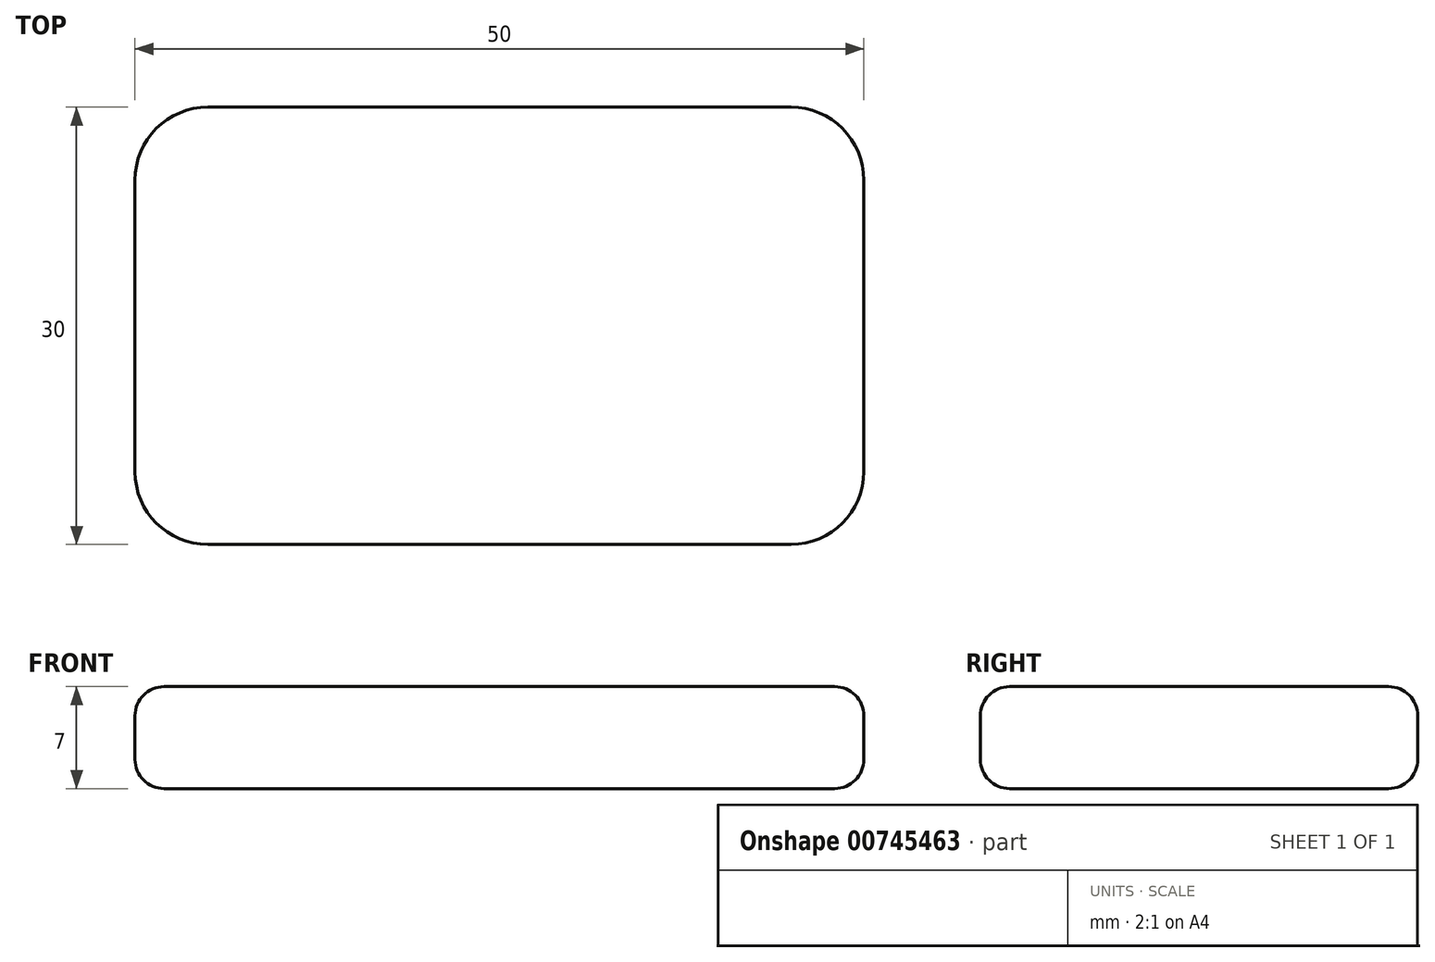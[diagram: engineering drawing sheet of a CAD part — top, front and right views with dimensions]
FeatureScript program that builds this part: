
annotation { "Feature Type Name" : "Feature", "Feature Type Description" : "" }
export const myFeature = defineFeature(function(context is Context, id is Id, definition is map)
    precondition{}
    {
        {
            var Q0;
            Q0=qCreatedBy(makeId("Top.planeOp"),FACE);
            var sketch = newSketch(context, id + "F0", { "sketchPlane" : qUnion([Q0])});
            skLineSegment(sketch, "E0.bottom", {"start": v(25, -15) * mm, "end": v(-25, -15) * mm});
            skLineSegment(sketch, "E0.top", {"start": v(25, 15) * mm, "end": v(-25, 15) * mm});
            skLineSegment(sketch, "E0.left", {"start": v(25, -15) * mm, "end": v(25, 15) * mm});
            skLineSegment(sketch, "E0.right", {"start": v(-25, -15) * mm, "end": v(-25, 15) * mm});
            skPoint(sketch, "E0.middle", {"position": v(0, 0) * mm});
            skSolve(sketch);
        }
        {
            var Q0;
            Q0=makeQuery(id+"F0.imprint","IMPRINT",FACE,{"disambiguationData":[TD([[makeQuery(id+"F0.imprint","IMPRINT",EDGE,{"derivedFrom":sQuery(id+"F0.wireOp",EDGE,"E0.bottom")}),-1.0]])]});
            extrude(context, id + "F1", {"entities" : qUnion([Q0]), "depth" : 7 * mm, "offsetDistance" : 25 * mm});
        }
        {
            var Q0;
            Q0=makeQuery(id+"F1.opExtrude","SWEPT_EDGE",EDGE,{"disambiguationData":[OSD([sQuery(id+"F0.wireOp",EDGE,"E0.bottom"),sQuery(id+"F0.wireOp",EDGE,"E0.left")])]});
            var Q1;
            Q1=makeQuery(id+"F1.opExtrude","SWEPT_EDGE",EDGE,{"disambiguationData":[OSD([sQuery(id+"F0.wireOp",EDGE,"E0.bottom"),sQuery(id+"F0.wireOp",EDGE,"E0.right")])]});
            var Q2;
            Q2=makeQuery(id+"F1.opExtrude","SWEPT_EDGE",EDGE,{"disambiguationData":[OSD([sQuery(id+"F0.wireOp",EDGE,"E0.top"),sQuery(id+"F0.wireOp",EDGE,"E0.left")])]});
            var Q3;
            Q3=makeQuery(id+"F1.opExtrude","SWEPT_EDGE",EDGE,{"disambiguationData":[OSD([sQuery(id+"F0.wireOp",EDGE,"E0.top"),sQuery(id+"F0.wireOp",EDGE,"E0.right")])]});
            fillet(context, id + "F2", {"entities" : qUnion([Q0, Q1, Q2, Q3]), "radius" : 5 * mm, "tangentPropagation" : true, "allowEdgeOverflow" : false});
        }
        {
            var Q0;
            Q0=makeQuery(id+"F1.opExtrude","CAP_EDGE",EDGE,{"disambiguationData":[OSD([sQuery(id+"F0.wireOp",EDGE,"E0.bottom")])],"isStart":false});
            var Q1;
            Q1=makeQuery(id+"F1.opExtrude","CAP_EDGE",EDGE,{"disambiguationData":[OSD([sQuery(id+"F0.wireOp",EDGE,"E0.bottom")])],"isStart":true});
            fillet(context, id + "F3", {"entities" : qUnion([Q0, Q1]), "radius" : 2 * mm, "tangentPropagation" : true, "allowEdgeOverflow" : false});
        }
    });
